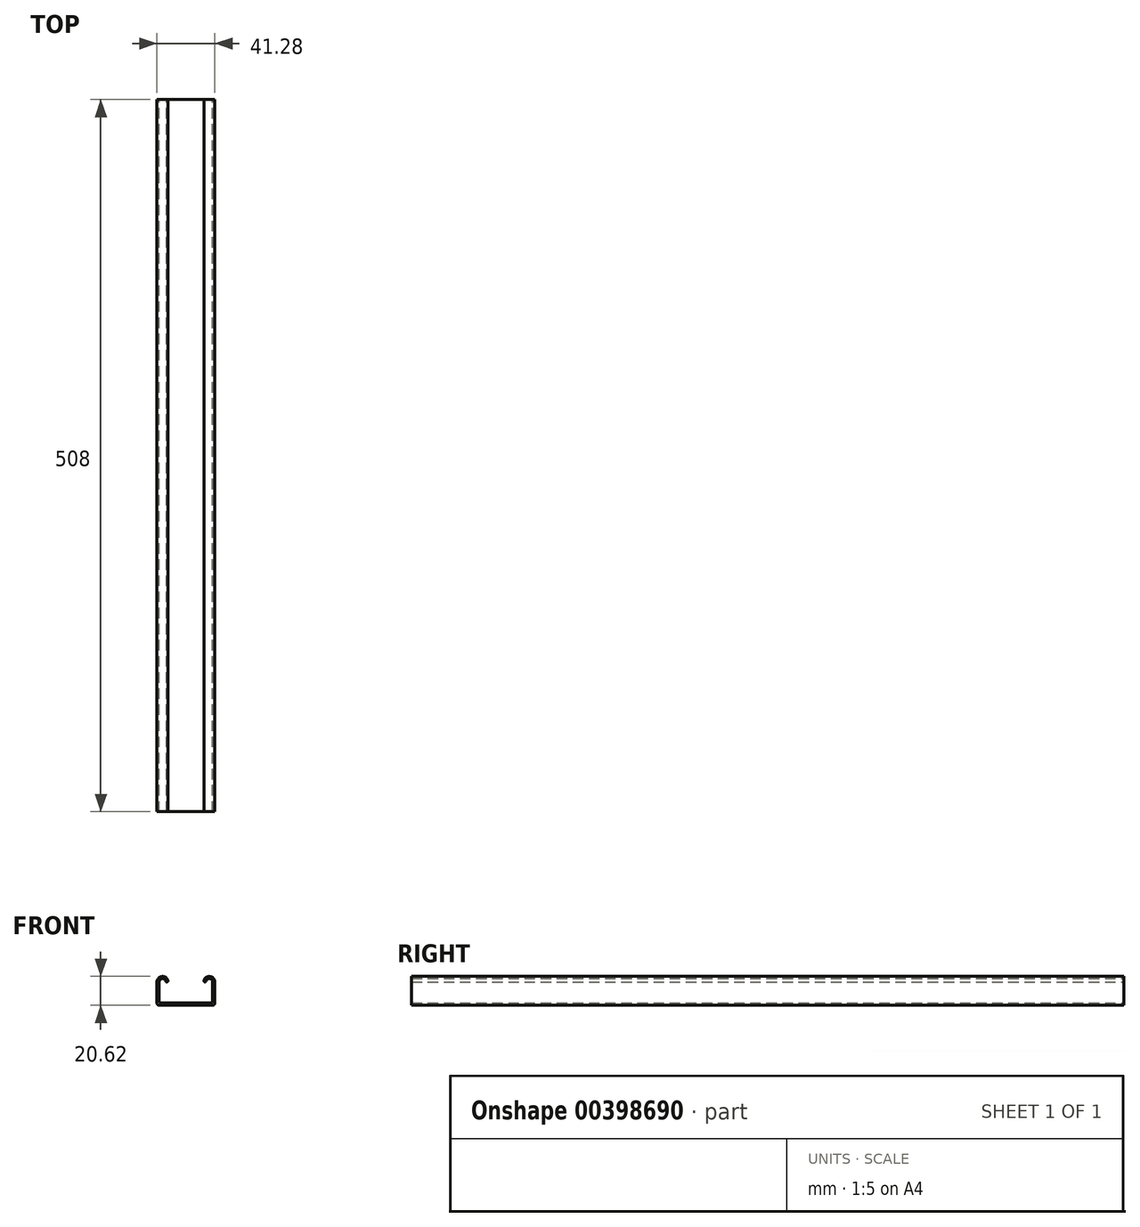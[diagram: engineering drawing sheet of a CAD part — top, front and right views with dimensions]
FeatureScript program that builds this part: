
annotation { "Feature Type Name" : "Feature", "Feature Type Description" : "" }
export const myFeature = defineFeature(function(context is Context, id is Id, definition is map)
    precondition{}
    {
        {
            var Q0;
            Q0=qCreatedBy(makeId("Front.planeOp"),FACE);
            var sketch = newSketch(context, id + "F0", { "sketchPlane" : qUnion([Q0])});
            skLineSegment(sketch, "E0.bottom", {"start": v(0, 0) * mm, "end": v(41.28, 0) * mm});
            skLineSegment(sketch, "E0.left", {"start": v(0, 0) * mm, "end": v(0, 16.66) * mm});
            skLineSegment(sketch, "E0.right", {"start": v(41.28, 0) * mm, "end": v(41.28, 16.66) * mm});
            skArc(sketch, "E1", {"start": v(7.92, 16.66) * mm, "mid": v(3.96, 20.62) * mm, "end": v(0, 16.66) * mm});
            skLineSegment(sketch, "E2.0", {"start": v(1.59, 1.59) * mm, "end": v(1.59, 16.66) * mm});
            skLineSegment(sketch, "E3.0", {"start": v(1.59, 1.59) * mm, "end": v(39.69, 1.59) * mm});
            skLineSegment(sketch, "E4.0", {"start": v(39.69, 1.59) * mm, "end": v(39.69, 16.66) * mm});
            skArc(sketch, "E5", {"start": v(6.34, 16.66) * mm, "mid": v(3.96, 19.04) * mm, "end": v(1.59, 16.66) * mm});
            skArc(sketch, "E6.MirrorC", {"start": v(33.35, 16.66) * mm, "mid": v(37.31, 20.62) * mm, "end": v(41.28, 16.66) * mm});
            skArc(sketch, "E7.MirrorC", {"start": v(34.94, 16.66) * mm, "mid": v(37.31, 19.04) * mm, "end": v(39.69, 16.66) * mm});
            skPoint(sketch, "E8.orphan", {"position": v(0, 20.62) * mm});
            skLineSegment(sketch, "E9", {"start": v(34.94, 16.66) * mm, "end": v(33.35, 16.66) * mm});
            skLineSegment(sketch, "E10.trimOffspring", {"start": v(1.59, 16.66) * mm, "end": v(0, 16.66) * mm});
            skLineSegment(sketch, "E11.trimOffspring", {"start": v(7.92, 16.66) * mm, "end": v(6.34, 16.66) * mm});
            skPoint(sketch, "E12.orphan", {"position": v(20.64, 20.62) * mm});
            skPoint(sketch, "E13.orphan", {"position": v(41.28, 16.66) * mm});
            skPoint(sketch, "E14.orphan", {"position": v(41.28, 20.62) * mm});
            skPoint(sketch, "E15.end.orphan", {"position": v(20.64, 0) * mm});
            skSolve(sketch);
        }
        {
            var Q0;
            Q0 = qSketchRegion(id + "F0", true);
            extrude(context, id + "F1", {"entities" : qUnion([Q0]), "endBound" : BoundingType.SYMMETRIC, "depth" : 508 * mm});
        }
        {
            var Q0;
            Q0=makeQuery(id+"F1.opExtrude","SWEPT_EDGE",EDGE,{"disambiguationData":[OSD([sQuery(id+"F0.wireOp",EDGE,"E0.bottom"),sQuery(id+"F0.wireOp",EDGE,"E0.left")])]});
            var Q1;
            Q1=makeQuery(id+"F1.opExtrude","SWEPT_EDGE",EDGE,{"disambiguationData":[OSD([sQuery(id+"F0.wireOp",EDGE,"E0.bottom"),sQuery(id+"F0.wireOp",EDGE,"E0.right")])]});
            var Q2;
            Q2=makeQuery(id+"F1.opExtrude","SWEPT_EDGE",EDGE,{"disambiguationData":[OSD([sQuery(id+"F0.wireOp",EDGE,"E3.0"),sQuery(id+"F0.wireOp",EDGE,"E4.0")])]});
            var Q3;
            Q3=makeQuery(id+"F1.opExtrude","SWEPT_EDGE",EDGE,{"disambiguationData":[OSD([sQuery(id+"F0.wireOp",EDGE,"E2.0"),sQuery(id+"F0.wireOp",EDGE,"E3.0")])]});
            fillet(context, id + "F2", {"entities" : qUnion([Q0, Q1, Q2, Q3]), "radius" : 1.59 * mm, "tangentPropagation" : true, "allowEdgeOverflow" : false});
        }
        {
            var Q0;
            Q0=makeQuery(id+"F1.opExtrude","SWEPT_EDGE",EDGE,{"disambiguationData":[OSD([sQuery(id+"F0.wireOp",EDGE,"E7.MirrorC"),sQuery(id+"F0.wireOp",EDGE,"E9")])]});
            var Q1;
            Q1=makeQuery(id+"F1.opExtrude","SWEPT_EDGE",EDGE,{"disambiguationData":[OSD([sQuery(id+"F0.wireOp",EDGE,"E6.MirrorC"),sQuery(id+"F0.wireOp",EDGE,"E9")])]});
            var Q2;
            Q2=makeQuery(id+"F1.opExtrude","SWEPT_EDGE",EDGE,{"disambiguationData":[OSD([sQuery(id+"F0.wireOp",EDGE,"E1"),sQuery(id+"F0.wireOp",EDGE,"E11.trimOffspring")])]});
            var Q3;
            Q3=makeQuery(id+"F1.opExtrude","SWEPT_EDGE",EDGE,{"disambiguationData":[OSD([sQuery(id+"F0.wireOp",EDGE,"E5"),sQuery(id+"F0.wireOp",EDGE,"E11.trimOffspring")])]});
            fillet(context, id + "F3", {"entities" : qUnion([Q0, Q1, Q2, Q3]), "radius" : 0.83 * mm, "tangentPropagation" : true, "allowEdgeOverflow" : false});
        }
    });
